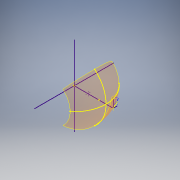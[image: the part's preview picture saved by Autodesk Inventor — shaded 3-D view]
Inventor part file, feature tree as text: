
AUTODESK INVENTOR PART (.ipt)
format: ipt  version: 2016 (Build 200138000, 138)  size: 130,048 bytes
history: native  units: mm
features: sketch x6, other x3, plane x2, revolve x1
ambient origin geometry x8: Origin, YZ Plane, XZ Plane, XY Plane, X Axis, Y Axis, Z Axis, Center Point
bodies: Body1 (feature_tree)
feature tree (12):
  sketch  "Sketch2"  dims[d2=6.981317mm]
  sketch  "3D Sketch1"
  sketch  "3D Sketch2"
  plane  "Work Plane1"
  sketch  "Sketch3"  dims[d3=17.453293mm]
  plane  "Work Plane2"
  sketch  "Sketch4"  dims[d4=2000.0mm d5=2000.0mm d6=1000.0mm d7=1000.0mm d8=350.0mm d9=350.0mm d10=100.0mm d11=200.0mm]
  sketch  "Sketch1"  dims[d0=800.0mm d1=17.453293mm]
  other  "Srf1"
  other  "Project to Surface1"
  other  "Project to Surface2"
  revolve  "RevolutionSrf1"  [1 undecoded]
note: 1 required parameter value undecoded (feature->parameter linkage not recoverable at this tier; creation-order binding heuristic only, values carry confidence <= 0.55)
